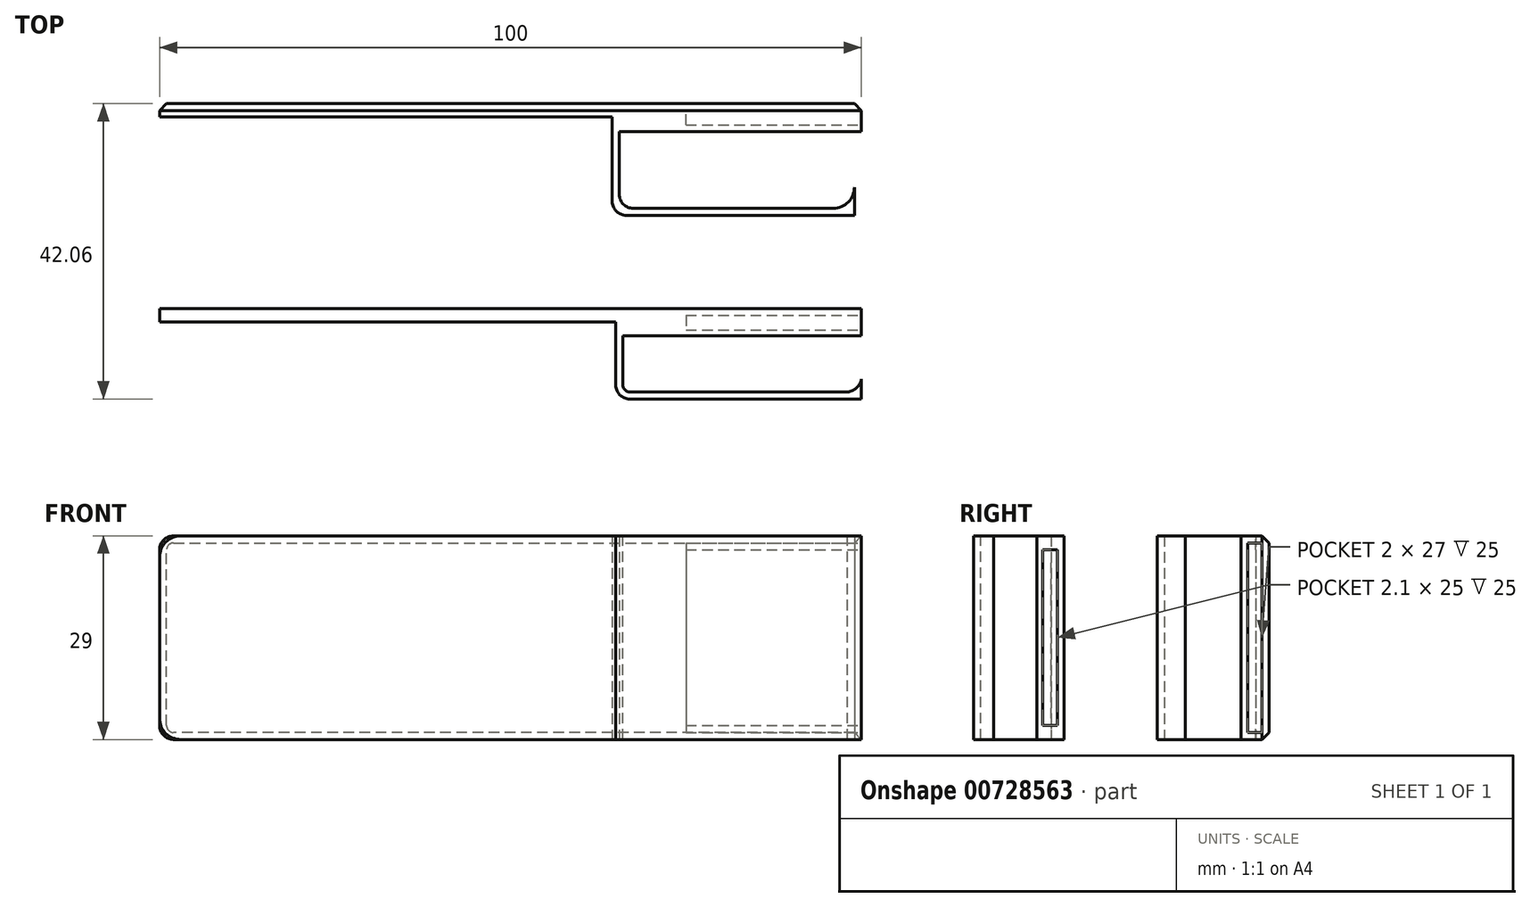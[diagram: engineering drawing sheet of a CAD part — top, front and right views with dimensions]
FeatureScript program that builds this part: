
annotation { "Feature Type Name" : "Feature", "Feature Type Description" : "" }
export const myFeature = defineFeature(function(context is Context, id is Id, definition is map)
    precondition{}
    {
        {
            var Q0;
            Q0=qCreatedBy(makeId("Front.planeOp"),FACE);
            var sketch = newSketch(context, id + "F0", { "sketchPlane" : qUnion([Q0])});
            skLineSegment(sketch, "E0.bottom", {"start": v(0, 0) * mm, "end": v(-97, 0) * mm});
            skLineSegment(sketch, "E0.top", {"start": v(0, 29) * mm, "end": v(-97, 29) * mm});
            skLineSegment(sketch, "E0.left", {"start": v(0, 0) * mm, "end": v(0, 29) * mm});
            skLineSegment(sketch, "E0.right", {"start": v(-100, 3) * mm, "end": v(-100, 26) * mm});
            skPoint(sketch, "E1.visualSharp", {"position": v(-100, 29) * mm});
            skArc(sketch, "E1.filletArc", {"start": v(-97, 29) * mm, "mid": v(-99.12, 28.12) * mm, "end": v(-100, 26) * mm});
            skPoint(sketch, "E2.visualSharp", {"position": v(-100, 0) * mm});
            skArc(sketch, "E2.filletArc", {"start": v(-100, 3) * mm, "mid": v(-99.12, 0.88) * mm, "end": v(-97, 0) * mm});
            skLineSegment(sketch, "E3", {"start": v(-35, 29) * mm, "end": v(-35, 0) * mm});
            skSolve(sketch);
        }
        {
            var Q0;
            Q0=makeQuery(id+"F0.imprint","IMPRINT",FACE,{"disambiguationData":[TD([[makeQuery(id+"F0.imprint","IMPRINT",EDGE,{"derivedFrom":sQuery(id+"F0.wireOp",EDGE,"E0.right")}),-1.0]])]});
            extrude(context, id + "F1", {"entities" : qUnion([Q0]), "depth" : 1.9 * mm, "offsetDistance" : 25 * mm});
        }
        {
            var Q0;
            {var subQ0=sQuery(id+"F0.wireOp",EDGE,"E0.left");Q0=makeQuery(id+"F0.imprint","IMPRINT",FACE,{"disambiguationData":[TD([[makeQuery(id+"F0.imprint","IMPRINT",EDGE,{"derivedFrom":subQ0}),1.0]])]});}
            extrude(context, id + "F2", {"entities" : qUnion([Q0]), "operationType" : NewBodyOperationType.ADD, "depth" : 12.9 * mm, "offsetDistance" : 25 * mm});
        }
        {
            var Q0;
            Q0=makeQuery(id+"F2.opExtrude","SWEPT_FACE",FACE,{"disambiguationData":[OSD([sQuery(id+"F0.wireOp",EDGE,"E0.left")])]});
            var sketch = newSketch(context, id + "F3", { "sketchPlane" : qUnion([Q0])});
            skLineSegment(sketch, "E4.bottom", {"start": v(-1, 27) * mm, "end": v(-3.1, 27) * mm});
            skLineSegment(sketch, "E4.top", {"start": v(-1, 2) * mm, "end": v(-3.1, 2) * mm});
            skLineSegment(sketch, "E4.left", {"start": v(-1, 27) * mm, "end": v(-1, 2) * mm});
            skLineSegment(sketch, "E4.right", {"start": v(-3.1, 27) * mm, "end": v(-3.1, 2) * mm});
            skSolve(sketch);
        }
        {
            var Q0;
            Q0=makeQuery(id+"F3.imprint","IMPRINT",FACE,{"disambiguationData":[TD([[makeQuery(id+"F3.imprint","IMPRINT",EDGE,{"derivedFrom":sQuery(id+"F3.wireOp",EDGE,"E4.bottom")}),1.0]])]});
            extrude(context, id + "F4", {"entities" : qUnion([Q0]), "operationType" : NewBodyOperationType.REMOVE, "oppositeDirection" : true, "depth" : 25 * mm, "offsetDistance" : 25 * mm});
        }
        {
            var Q0;
            Q0=makeQuery(id+"F2.opExtrude","CAP_EDGE",EDGE,{"disambiguationData":[OSD([sQuery(id+"F0.wireOp",EDGE,"E3")])],"isStart":false});
            fillet(context, id + "F5", {"entities" : qUnion([Q0]), "radius" : 2 * mm, "tangentPropagation" : true, "allowEdgeOverflow" : false});
        }
        {
            var Q0;
            {var subQ0=sQuery(id+"F0.wireOp",EDGE,"E0.top");Q0=makeQuery(id+"F2.boolean.opBoolean","MERGE",FACE,{"derivedFrom":[makeQuery(id+"F1.opExtrude","SWEPT_FACE",FACE,{"disambiguationData":[OSD([subQ0])]}),makeQuery(id+"F2.opExtrude","SWEPT_FACE",FACE,{"disambiguationData":[OSD([subQ0])]})]});}
            var sketch = newSketch(context, id + "F6", { "sketchPlane" : qUnion([Q0])});
            skLineSegment(sketch, "E5.0", {"start": v(-34, -10.9) * mm, "end": v(-34, -3.9) * mm});
            skArc(sketch, "E5.1", {"start": v(-34, -10.9) * mm, "mid": v(-33.7, -11.6) * mm, "end": v(-33, -11.9) * mm});
            skLineSegment(sketch, "E5.2", {"start": v(0, -11.9) * mm, "end": v(-33, -11.9) * mm});
            skLineSegment(sketch, "E6", {"start": v(-34, -3.9) * mm, "end": v(0, -3.9) * mm});
            skArc(sketch, "E7", {"start": v(-2.5, -11.9) * mm, "mid": v(-0.55, -11.16) * mm, "end": v(0, -9.16) * mm});
            skSolve(sketch);
        }
        {
            var Q0;
            Q0=makeQuery(id+"F6.imprint","IMPRINT",FACE,{"disambiguationData":[TD([[makeQuery(id+"F6.imprint","IMPRINT",EDGE,{"derivedFrom":sQuery(id+"F6.wireOp",EDGE,"E5.0")}),-1.0]])]});
            extrude(context, id + "F7", {"entities" : qUnion([Q0]), "operationType" : NewBodyOperationType.REMOVE, "oppositeDirection" : true, "depth" : 29 * mm, "offsetDistance" : 25 * mm});
        }
        {
            var Q0;
            Q0=qCreatedBy(makeId("Top.planeOp"),FACE);
            var sketch = newSketch(context, id + "F8", { "sketchPlane" : qUnion([Q0])});
            skLineSegment(sketch, "E8", {"start": v(0, 29.16) * mm, "end": v(-100, 29.16) * mm});
            skLineSegment(sketch, "E9", {"start": v(-100, 29.16) * mm, "end": v(-100, 27.26) * mm});
            skLineSegment(sketch, "E10", {"start": v(-100, 27.26) * mm, "end": v(-35.5, 27.26) * mm});
            skLineSegment(sketch, "E11", {"start": v(-35.5, 27.26) * mm, "end": v(-35.5, 15.26) * mm});
            skLineSegment(sketch, "E12", {"start": v(-33.5, 13.26) * mm, "end": v(-1, 13.26) * mm});
            skLineSegment(sketch, "E13", {"start": v(-1, 13.26) * mm, "end": v(-1, 17.26) * mm});
            skLineSegment(sketch, "E14", {"start": v(0, 29.16) * mm, "end": v(0, 25.16) * mm});
            skLineSegment(sketch, "E15", {"start": v(0, 25.16) * mm, "end": v(-34.5, 25.16) * mm});
            skLineSegment(sketch, "E16", {"start": v(-34.5, 25.16) * mm, "end": v(-34.5, 16.26) * mm});
            skLineSegment(sketch, "E17", {"start": v(-32.5, 14.26) * mm, "end": v(-4, 14.26) * mm});
            skArc(sketch, "E18", {"start": v(-4, 14.26) * mm, "mid": v(-1.88, 15.14) * mm, "end": v(-1, 17.26) * mm});
            skPoint(sketch, "E19.visualSharp", {"position": v(-34.5, 14.26) * mm});
            skArc(sketch, "E19.filletArc", {"start": v(-34.5, 16.26) * mm, "mid": v(-33.91, 14.84) * mm, "end": v(-32.5, 14.26) * mm});
            skPoint(sketch, "E20.visualSharp", {"position": v(-35.5, 13.26) * mm});
            skArc(sketch, "E20.filletArc", {"start": v(-35.5, 15.26) * mm, "mid": v(-34.91, 13.84) * mm, "end": v(-33.5, 13.26) * mm});
            skSolve(sketch);
        }
        {
            var Q0;
            Q0=makeQuery(id+"F8.imprint","IMPRINT",FACE,{"disambiguationData":[TD([[makeQuery(id+"F8.imprint","IMPRINT",EDGE,{"derivedFrom":sQuery(id+"F8.wireOp",EDGE,"E8")}),1.0]])]});
            extrude(context, id + "F9", {"entities" : qUnion([Q0]), "depth" : 29 * mm, "offsetDistance" : 25 * mm});
        }
        {
            var Q0;
            Q0=makeQuery(id+"F9.opExtrude","SWEPT_FACE",FACE,{"disambiguationData":[OSD([sQuery(id+"F8.wireOp",EDGE,"E14")])]});
            var sketch = newSketch(context, id + "F10", { "sketchPlane" : qUnion([Q0])});
            skLineSegment(sketch, "E21.0", {"start": v(26.16, 1) * mm, "end": v(28.16, 1) * mm});
            skLineSegment(sketch, "E21.1", {"start": v(26.16, 28) * mm, "end": v(26.16, 1) * mm});
            skLineSegment(sketch, "E21.2", {"start": v(28.16, 28) * mm, "end": v(26.16, 28) * mm});
            skLineSegment(sketch, "E21.3", {"start": v(28.16, 1) * mm, "end": v(28.16, 28) * mm});
            skSolve(sketch);
        }
        {
            var Q0;
            Q0=makeQuery(id+"F10.imprint","IMPRINT",FACE,{"disambiguationData":[TD([[makeQuery(id+"F10.imprint","IMPRINT",EDGE,{"derivedFrom":sQuery(id+"F10.wireOp",EDGE,"E21.0")}),1.0]])]});
            extrude(context, id + "F11", {"entities" : qUnion([Q0]), "operationType" : NewBodyOperationType.REMOVE, "oppositeDirection" : true, "depth" : 25 * mm, "offsetDistance" : 25 * mm});
        }
        {
            var Q0;
            Q0=makeQuery(id+"F9.opExtrude","SWEPT_BODY",BODY,{"disambiguationData":[OSD([sQuery(id+"F8.wireOp",EDGE,"E8"),sQuery(id+"F8.wireOp",EDGE,"E9"),sQuery(id+"F8.wireOp",EDGE,"E10"),sQuery(id+"F8.wireOp",EDGE,"E11"),sQuery(id+"F8.wireOp",EDGE,"E12"),sQuery(id+"F8.wireOp",EDGE,"E13"),sQuery(id+"F8.wireOp",EDGE,"E14"),sQuery(id+"F8.wireOp",EDGE,"E15"),sQuery(id+"F8.wireOp",EDGE,"E16"),sQuery(id+"F8.wireOp",EDGE,"E17"),sQuery(id+"F8.wireOp",EDGE,"E18"),sQuery(id+"F8.wireOp",EDGE,"E19.filletArc"),sQuery(id+"F8.wireOp",EDGE,"E20.filletArc")])]});
            transform(context, id + "F12", {"entities" : qUnion([Q0]), "transformType" : TransformType.TRANSLATION_3D, "dx" : 0 * mm, "dy" : 30 * mm, "dz" : 0 * mm, "makeCopy" : true});
        }
        {
            var Q0;
            Q0=makeQuery(id+"F12.opPattern","COPY",BODY,{"derivedFrom":makeQuery(id+"F9.opExtrude","SWEPT_BODY",BODY,{"disambiguationData":[OSD([sQuery(id+"F8.wireOp",EDGE,"E8"),sQuery(id+"F8.wireOp",EDGE,"E9"),sQuery(id+"F8.wireOp",EDGE,"E10"),sQuery(id+"F8.wireOp",EDGE,"E11"),sQuery(id+"F8.wireOp",EDGE,"E12"),sQuery(id+"F8.wireOp",EDGE,"E13"),sQuery(id+"F8.wireOp",EDGE,"E14"),sQuery(id+"F8.wireOp",EDGE,"E15"),sQuery(id+"F8.wireOp",EDGE,"E16"),sQuery(id+"F8.wireOp",EDGE,"E17"),sQuery(id+"F8.wireOp",EDGE,"E18"),sQuery(id+"F8.wireOp",EDGE,"E19.filletArc"),sQuery(id+"F8.wireOp",EDGE,"E20.filletArc")])]}),"instanceName":"1"});
            deleteBodies(context, id + "F13", {"entities" : qUnion([Q0])});
        }
        {
            var Q0;
            Q0=makeQuery(id+"F9.opExtrude","CAP_EDGE",EDGE,{"disambiguationData":[OSD([sQuery(id+"F8.wireOp",EDGE,"E9")])],"isStart":false});
            var Q1;
            Q1=makeQuery(id+"F9.opExtrude","CAP_EDGE",EDGE,{"disambiguationData":[OSD([sQuery(id+"F8.wireOp",EDGE,"E9")])],"isStart":true});
            fillet(context, id + "F14", {"entities" : qUnion([Q0, Q1]), "radius" : 2 * mm, "tangentPropagation" : true, "allowEdgeOverflow" : false});
        }
        {
            var Q0;
            Q0=makeQuery(id+"F9.opExtrude","SWEPT_FACE",FACE,{"disambiguationData":[OSD([sQuery(id+"F8.wireOp",EDGE,"E8")])]});
            chamfer(context, id + "F15", {"entities" : qUnion([Q0]), "width" : 1 * mm, "tangentPropagation" : true});
        }
    });
